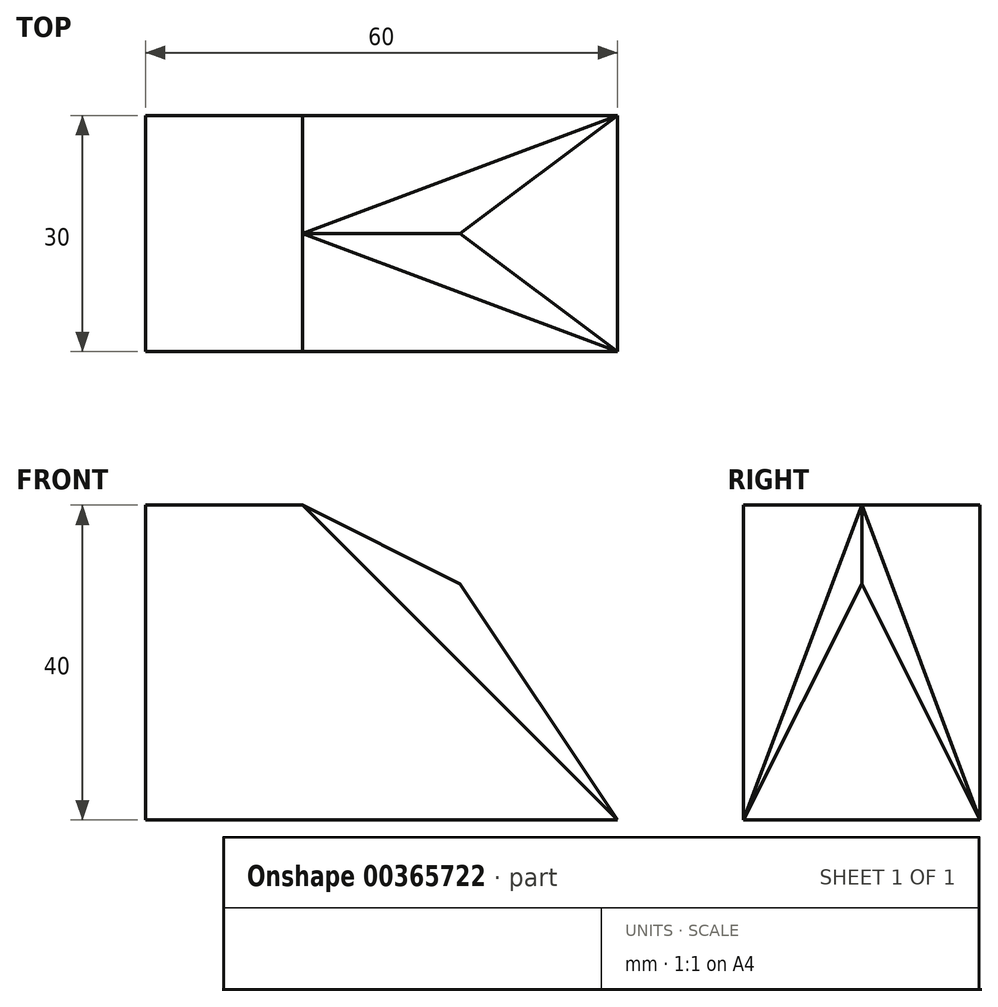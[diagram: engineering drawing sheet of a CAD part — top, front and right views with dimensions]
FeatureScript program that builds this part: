
annotation { "Feature Type Name" : "Feature", "Feature Type Description" : "" }
export const myFeature = defineFeature(function(context is Context, id is Id, definition is map)
    precondition{}
    {
        {
            var Q0;
            Q0=qCreatedBy(makeId("Front.planeOp"),FACE);
            var sketch = newSketch(context, id + "F0", { "sketchPlane" : qUnion([Q0])});
            skLineSegment(sketch, "E0", {"start": v(0, 0) * mm, "end": v(0, 40) * mm});
            skLineSegment(sketch, "E1", {"start": v(0, 40) * mm, "end": v(20, 40) * mm});
            skLineSegment(sketch, "E2", {"start": v(20, 40) * mm, "end": v(60, 0) * mm});
            skLineSegment(sketch, "E3", {"start": v(60, 0) * mm, "end": v(0, 0) * mm});
            skSolve(sketch);
        }
        {
            var Q0;
            Q0=makeQuery(id+"F0.imprint","IMPRINT",FACE,{"disambiguationData":[TD([[makeQuery(id+"F0.imprint","IMPRINT",EDGE,{"derivedFrom":sQuery(id+"F0.wireOp",EDGE,"E0")}),-1.0]])]});
            extrude(context, id + "F1", {"entities" : qUnion([Q0]), "endBound" : BoundingType.SYMMETRIC, "depth" : 30 * mm});
        }
        {
            var Q0;
            Q0=qCreatedBy(makeId("Front.planeOp"),FACE);
            var sketch = newSketch(context, id + "F2", { "sketchPlane" : qUnion([Q0])});
            skPoint(sketch, "E4", {"position": v(40, 30) * mm});
            skSolve(sketch);
        }
        {
            var Q0;
            Q0=makeQuery(id+"F1.opExtrude","SWEPT_FACE",FACE,{"disambiguationData":[OSD([sQuery(id+"F0.wireOp",EDGE,"E2")])]});
            var sketch = newSketch(context, id + "F3", { "sketchPlane" : qUnion([Q0])});
            skLineSegment(sketch, "E5", {"start": v(15, -42.43) * mm, "end": v(0, 14.14) * mm});
            skLineSegment(sketch, "E6", {"start": v(0, 14.14) * mm, "end": v(-15, -42.43) * mm});
            skLineSegment(sketch, "E7", {"start": v(-15, -42.43) * mm, "end": v(15, -42.43) * mm});
            skSolve(sketch);
        }
        {
            var Q1;
            Q1=makeQuery(id+"F3.imprint","IMPRINT",FACE,{"disambiguationData":[TD([[makeQuery(id+"F3.imprint","IMPRINT",EDGE,{"derivedFrom":sQuery(id+"F3.wireOp",EDGE,"E5")}),1.0]])]});
            var Q2;
            Q2=sQuery(id+"F2.wireOp",VERTEX,"E4");
            loft(context, id + "F4", {"operationType" : NewBodyOperationType.ADD, "sheetProfilesArray" : [{ "sheetProfileEntities" : qUnion([Q1]) }, { "sheetProfileEntities" : qUnion([Q2]) }]});
        }
    });
